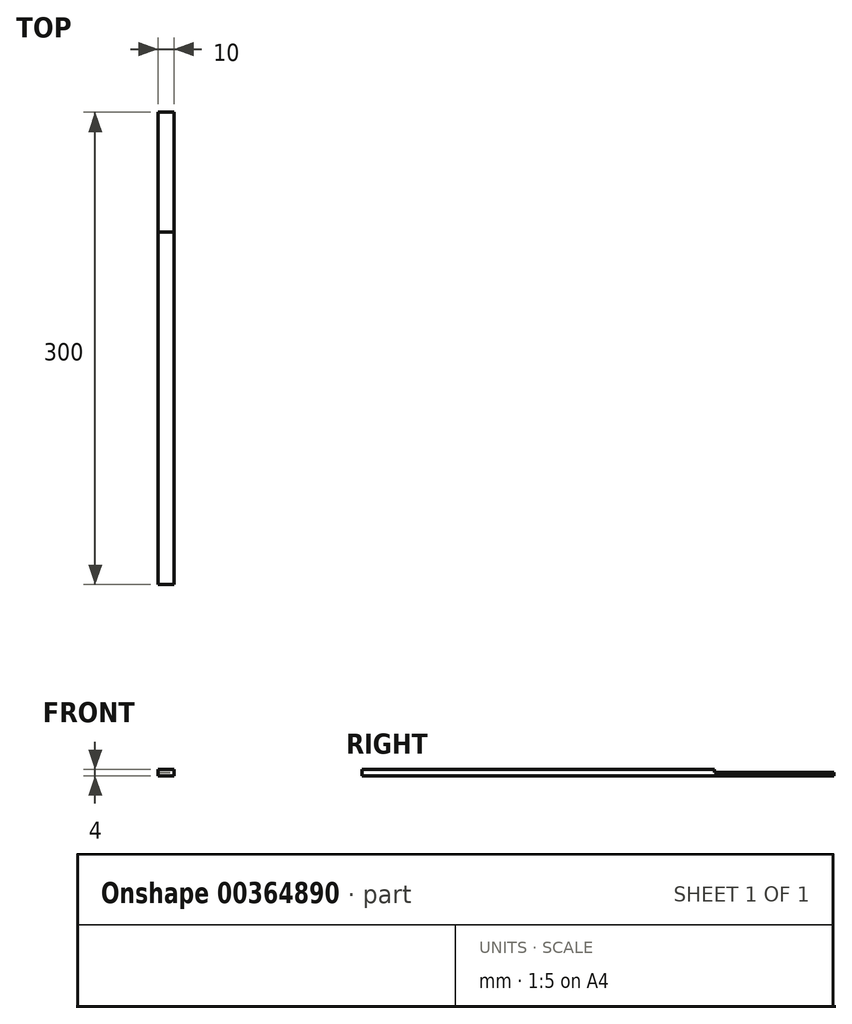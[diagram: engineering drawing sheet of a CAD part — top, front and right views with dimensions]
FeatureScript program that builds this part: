
annotation { "Feature Type Name" : "Feature", "Feature Type Description" : "" }
export const myFeature = defineFeature(function(context is Context, id is Id, definition is map)
    precondition{}
    {
        {
            var Q0;
            Q0=qCreatedBy(makeId("Top.planeOp"),FACE);
            var sketch = newSketch(context, id + "F0", { "sketchPlane" : qUnion([Q0])});
            skLineSegment(sketch, "E0.bottom", {"start": v(0, 0) * mm, "end": v(10, 0) * mm});
            skLineSegment(sketch, "E0.top", {"start": v(0, 300) * mm, "end": v(10, 300) * mm});
            skLineSegment(sketch, "E0.left", {"start": v(0, 0) * mm, "end": v(0, 300) * mm});
            skLineSegment(sketch, "E0.right", {"start": v(10, 0) * mm, "end": v(10, 300) * mm});
            skSolve(sketch);
        }
        {
            var Q0;
            Q0=makeQuery(id+"F0.imprint","IMPRINT",FACE,{"disambiguationData":[TD([[makeQuery(id+"F0.imprint","IMPRINT",EDGE,{"derivedFrom":sQuery(id+"F0.wireOp",EDGE,"E0.bottom")}),1.0]])]});
            var sketch = newSketch(context, id + "F1", { "sketchPlane" : qUnion([Q0])});
            skLineSegment(sketch, "E1", {"start": v(0, 224) * mm, "end": v(9.73, 224) * mm});
            skSolve(sketch);
        }
        {
            var Q0;
            {var subQ1=makeQuery(id+"F0.imprint","IMPRINT",EDGE,{"derivedFrom":sQuery(id+"F0.wireOp",EDGE,"E0.bottom")});Q0=makeQuery(id+"F1.imprint","IMPRINT",FACE,{"disambiguationData":[TD([[makeQuery(id+"F1.imprint","IMPRINT",EDGE,{"derivedFrom":subQ1}),1.0]])]});}
            extrude(context, id + "F2", {"entities" : qUnion([Q0]), "depth" : 2 * mm});
        }
        {
            var Q0;
            Q0=makeQuery(id+"F2.opExtrude","CAP_FACE",FACE,{"disambiguationData":[OSD([sQuery(id+"F0.wireOp",EDGE,"E0.bottom"),sQuery(id+"F0.wireOp",EDGE,"E0.top"),sQuery(id+"F0.wireOp",EDGE,"E0.left"),sQuery(id+"F0.wireOp",EDGE,"E0.right")])],"isStart":false});
            var sketch = newSketch(context, id + "F3", { "sketchPlane" : qUnion([Q0])});
            skLineSegment(sketch, "E2", {"start": v(0, 224) * mm, "end": v(10, 224) * mm});
            skSolve(sketch);
        }
        {
            var Q0;
            {var subQ0=sQuery(id+"F3.wireOp",EDGE,"E2");Q0=makeQuery(id+"F3.imprint","IMPRINT",FACE,{"disambiguationData":[TD([[makeQuery(id+"F3.imprint","IMPRINT",EDGE,{"derivedFrom":subQ0}),-1.0]])]});}
            extrude(context, id + "F4", {"entities" : qUnion([Q0]), "operationType" : NewBodyOperationType.ADD, "depth" : 2 * mm});
        }
    });
